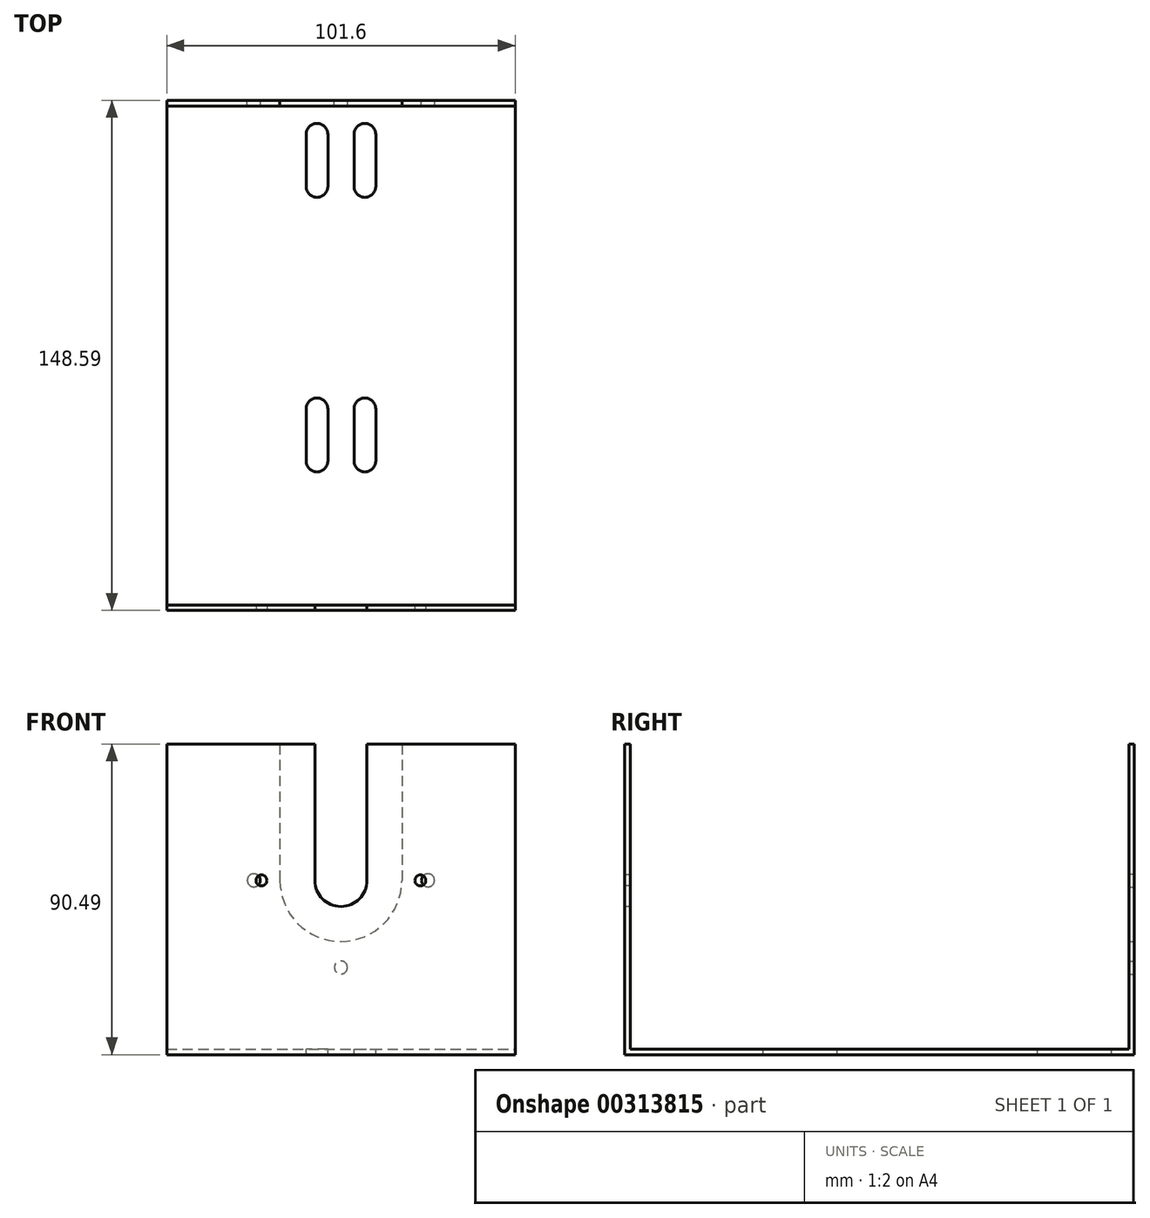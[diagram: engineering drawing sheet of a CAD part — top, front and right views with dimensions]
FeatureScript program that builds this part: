
annotation { "Feature Type Name" : "Feature", "Feature Type Description" : "" }
export const myFeature = defineFeature(function(context is Context, id is Id, definition is map)
    precondition{}
    {
        {
            var Q0;
            Q0=qCreatedBy(makeId("Top.planeOp"),FACE);
            var sketch = newSketch(context, id + "F0", { "sketchPlane" : qUnion([Q0])});
            skLineSegment(sketch, "E0.bottom", {"start": v(0, 0) * mm, "end": v(101.6, 0) * mm});
            skLineSegment(sketch, "E0.top", {"start": v(0, 148.6) * mm, "end": v(101.6, 148.6) * mm});
            skLineSegment(sketch, "E0.left", {"start": v(0, 0) * mm, "end": v(0, 148.6) * mm});
            skLineSegment(sketch, "E0.right", {"start": v(101.6, 0) * mm, "end": v(101.6, 148.6) * mm});
            skSolve(sketch);
        }
        {
            var Q0;
            Q0 = qSketchRegion(id + "F0", true);
            extrude(context, id + "F1", {"entities" : qUnion([Q0]), "depth" : 1.59 * mm});
        }
        {
            var Q0;
            Q0=makeQuery(id+"F1.opExtrude","CAP_FACE",FACE,{"disambiguationData":[OSD([sQuery(id+"F0.wireOp",EDGE,"E0.bottom"),sQuery(id+"F0.wireOp",EDGE,"E0.top"),sQuery(id+"F0.wireOp",EDGE,"E0.left"),sQuery(id+"F0.wireOp",EDGE,"E0.right")])],"isStart":false});
            var sketch = newSketch(context, id + "F2", { "sketchPlane" : qUnion([Q0])});
            skLineSegment(sketch, "E1.bottom", {"start": v(0, 148.6) * mm, "end": v(101.6, 148.6) * mm});
            skLineSegment(sketch, "E1.top", {"start": v(0, 147) * mm, "end": v(101.6, 147) * mm});
            skLineSegment(sketch, "E1.left", {"start": v(0, 148.6) * mm, "end": v(0, 147) * mm});
            skLineSegment(sketch, "E1.right", {"start": v(101.6, 148.6) * mm, "end": v(101.6, 147) * mm});
            skLineSegment(sketch, "E2.bottom", {"start": v(0, 0) * mm, "end": v(101.6, 0) * mm});
            skLineSegment(sketch, "E2.top", {"start": v(0, 1.59) * mm, "end": v(101.6, 1.59) * mm});
            skLineSegment(sketch, "E2.left", {"start": v(0, 0) * mm, "end": v(0, 1.59) * mm});
            skLineSegment(sketch, "E2.right", {"start": v(101.6, 0) * mm, "end": v(101.6, 1.59) * mm});
            skSolve(sketch);
        }
        {
            var Q0;
            Q0 = qSketchRegion(id + "F2", true);
            extrude(context, id + "F3", {"entities" : qUnion([Q0]), "operationType" : NewBodyOperationType.ADD, "depth" : 88.9 * mm});
        }
        {
            var Q0;
            Q0=makeQuery(id+"F3.boolean.opBoolean","MERGE",FACE,{"derivedFrom":[makeQuery(id+"F1.opExtrude","SWEPT_FACE",FACE,{"disambiguationData":[OSD([sQuery(id+"F0.wireOp",EDGE,"E0.top")])]}),makeQuery(id+"F3.opExtrude","SWEPT_FACE",FACE,{"disambiguationData":[OSD([sQuery(id+"F2.wireOp",EDGE,"E1.bottom")])]})]});
            var sketch = newSketch(context, id + "F4", { "sketchPlane" : qUnion([Q0])});
            skCircle(sketch, "E3", {"center": v(-50.8, 50.8) * mm, "radius": 38.1 * mm, "construction": true});
            skPoint(sketch, "E3.centerSnap0", {"position": v(-50.8, 90.49) * mm});
            skSolve(sketch);
        }
        {
            var Q0;
            {var subQ0=sQuery(id+"F0.wireOp",EDGE,"E0.top");Q0=makeQuery(id+"F4.imprint","IMPRINT",FACE,{"disambiguationData":[TD([[makeQuery(id+"F4.imprint","IMPRINT",EDGE,{"derivedFrom":makeQuery(id+"F1.opExtrude","CAP_EDGE",EDGE,{"disambiguationData":[OSD([subQ0])],"isStart":true})}),-1.0]])]});}
            var sketch = newSketch(context, id + "F5", { "sketchPlane" : qUnion([Q0])});
            skCircle(sketch, "E4.0", {"center": v(-50.8, 50.8) * mm, "radius": 38.1 * mm, "construction": true});
            skLineSegment(sketch, "E5", {"start": v(-50.8, -11.96) * mm, "end": v(-50.8, 107.1) * mm, "construction": true});
            skCircle(sketch, "E6", {"center": v(-50.8, 50.8) * mm, "radius": 17.78 * mm});
            skLineSegment(sketch, "E7", {"start": v(-68.58, 50.8) * mm, "end": v(-68.58, 90.49) * mm});
            skLineSegment(sketch, "E8", {"start": v(-33.02, 50.8) * mm, "end": v(-33.02, 90.49) * mm});
            skLineSegment(sketch, "E9", {"start": v(-68.58, 90.49) * mm, "end": v(-33.02, 90.49) * mm});
            skLineSegment(sketch, "E10", {"start": v(-105.94, 50.8) * mm, "end": v(8.17, 50.8) * mm, "construction": true});
            skCircle(sketch, "E11", {"center": v(-50.8, 25.4) * mm, "radius": 1.9 * mm});
            skCircle(sketch, "E12", {"center": v(-25.4, 50.8) * mm, "radius": 1.9 * mm});
            skCircle(sketch, "E13", {"center": v(-76.2, 50.8) * mm, "radius": 1.9 * mm});
            skSolve(sketch);
        }
        {
            var Q0;
            Q0 = qSketchRegion(id + "F5", true);
            extrude(context, id + "F6", {"entities" : qUnion([Q0]), "operationType" : NewBodyOperationType.REMOVE, "endBound" : BoundingType.UP_TO_NEXT, "oppositeDirection" : true, "depth" : 25.4 * mm});
        }
        {
            var Q0;
            Q0=makeQuery(id+"F3.boolean.opBoolean","MERGE",FACE,{"derivedFrom":[makeQuery(id+"F1.opExtrude","SWEPT_FACE",FACE,{"disambiguationData":[OSD([sQuery(id+"F0.wireOp",EDGE,"E0.bottom")])]}),makeQuery(id+"F3.opExtrude","SWEPT_FACE",FACE,{"disambiguationData":[OSD([sQuery(id+"F2.wireOp",EDGE,"E2.bottom")])]})]});
            var sketch = newSketch(context, id + "F7", { "sketchPlane" : qUnion([Q0])});
            skCircle(sketch, "E14.0", {"center": v(50.8, 50.8) * mm, "radius": 38.1 * mm, "construction": true});
            skCircle(sketch, "E15", {"center": v(50.8, 50.8) * mm, "radius": 7.62 * mm});
            skLineSegment(sketch, "E16", {"start": v(43.18, 50.8) * mm, "end": v(43.18, 90.49) * mm});
            skLineSegment(sketch, "E17", {"start": v(58.42, 50.8) * mm, "end": v(58.42, 90.49) * mm});
            skLineSegment(sketch, "E18", {"start": v(58.42, 90.49) * mm, "end": v(43.18, 90.49) * mm});
            skLineSegment(sketch, "E19", {"start": v(50.8, 96.93) * mm, "end": v(50.8, -8.53) * mm, "construction": true});
            skPoint(sketch, "E19.endSnap0", {"position": v(50.8, 5.08) * mm});
            skLineSegment(sketch, "E20", {"start": v(-8.65, 50.8) * mm, "end": v(115.7, 50.8) * mm, "construction": true});
            skCircle(sketch, "E21", {"center": v(73.98, 50.8) * mm, "radius": 1.59 * mm});
            skCircle(sketch, "E22.MirrorC", {"center": v(27.62, 50.8) * mm, "radius": 1.59 * mm});
            skSolve(sketch);
        }
        {
            var Q0;
            Q0 = qSketchRegion(id + "F7", true);
            extrude(context, id + "F8", {"entities" : qUnion([Q0]), "operationType" : NewBodyOperationType.REMOVE, "endBound" : BoundingType.UP_TO_NEXT, "oppositeDirection" : true, "depth" : 25.4 * mm});
        }
        {
            var Q0;
            Q0=makeQuery(id+"F1.opExtrude","CAP_FACE",FACE,{"disambiguationData":[OSD([sQuery(id+"F0.wireOp",EDGE,"E0.bottom"),sQuery(id+"F0.wireOp",EDGE,"E0.top"),sQuery(id+"F0.wireOp",EDGE,"E0.left"),sQuery(id+"F0.wireOp",EDGE,"E0.right")])],"isStart":false});
            var sketch = newSketch(context, id + "F9", { "sketchPlane" : qUnion([Q0])});
            skLineSegment(sketch, "E23", {"start": v(50.8, 141.92) * mm, "end": v(50.8, 6.67) * mm, "construction": true});
            skLineSegment(sketch, "E24", {"start": v(0, 40.32) * mm, "end": v(101.6, 40.32) * mm, "construction": true});
            skLineSegment(sketch, "E25", {"start": v(50.8, 49.85) * mm, "end": v(38.1, 49.85) * mm, "construction": true});
            skLineSegment(sketch, "E26", {"start": v(50.8, 43.5) * mm, "end": v(38.1, 43.5) * mm, "construction": true});
            skLineSegment(sketch, "E27", {"start": v(50.8, 40.32) * mm, "end": v(50.8, 141.92) * mm, "construction": true});
            skLineSegment(sketch, "E28", {"start": v(0, 91.12) * mm, "end": v(101.6, 91.12) * mm, "construction": true});
            skPoint(sketch, "E28.startSnap0", {"position": v(50.8, 91.12) * mm});
            skArc(sketch, "E29", {"start": v(38.1, 49.85) * mm, "mid": v(34.92, 46.67) * mm, "end": v(38.1, 43.5) * mm, "construction": true});
            skLineSegment(sketch, "E30.MirrorCS", {"start": v(50.8, 49.85) * mm, "end": v(63.5, 49.85) * mm, "construction": true});
            skLineSegment(sketch, "E31.MirrorCS", {"start": v(50.8, 43.5) * mm, "end": v(63.5, 43.5) * mm, "construction": true});
            skArc(sketch, "E32.MirrorCS", {"start": v(63.5, 49.85) * mm, "mid": v(66.68, 46.67) * mm, "end": v(63.5, 43.5) * mm, "construction": true});
            skArc(sketch, "E33.MirrorCS", {"start": v(63.5, 132.4) * mm, "mid": v(66.68, 135.57) * mm, "end": v(63.5, 138.75) * mm, "construction": true});
            skLineSegment(sketch, "E34.MirrorCS", {"start": v(50.8, 138.75) * mm, "end": v(63.5, 138.75) * mm, "construction": true});
            skArc(sketch, "E35.MirrorCS", {"start": v(38.1, 132.4) * mm, "mid": v(34.92, 135.57) * mm, "end": v(38.1, 138.75) * mm, "construction": true});
            skLineSegment(sketch, "E36.MirrorCS", {"start": v(50.8, 138.75) * mm, "end": v(38.1, 138.75) * mm, "construction": true});
            skLineSegment(sketch, "E37.MirrorCS", {"start": v(50.8, 132.4) * mm, "end": v(38.1, 132.4) * mm, "construction": true});
            skLineSegment(sketch, "E38.MirrorCS", {"start": v(50.8, 132.4) * mm, "end": v(63.5, 132.4) * mm, "construction": true});
            skLineSegment(sketch, "E39.bottom", {"start": v(40.64, 138.75) * mm, "end": v(46.99, 138.75) * mm});
            skLineSegment(sketch, "E39.top", {"start": v(40.64, 123.5) * mm, "end": v(46.99, 123.5) * mm});
            skLineSegment(sketch, "E39.left", {"start": v(40.64, 138.75) * mm, "end": v(40.64, 123.5) * mm});
            skLineSegment(sketch, "E39.right", {"start": v(46.99, 138.75) * mm, "end": v(46.99, 123.5) * mm});
            skArc(sketch, "E40", {"start": v(46.99, 138.75) * mm, "mid": v(43.81, 141.92) * mm, "end": v(40.64, 138.75) * mm});
            skArc(sketch, "E41", {"start": v(40.64, 123.5) * mm, "mid": v(43.81, 120.33) * mm, "end": v(46.99, 123.5) * mm});
            skLineSegment(sketch, "E42.MirrorCS", {"start": v(60.96, 138.75) * mm, "end": v(54.61, 138.75) * mm});
            skLineSegment(sketch, "E43.MirrorCS", {"start": v(54.61, 138.75) * mm, "end": v(54.61, 123.5) * mm});
            skArc(sketch, "E44.MirrorCS", {"start": v(60.96, 123.5) * mm, "mid": v(57.79, 120.33) * mm, "end": v(54.61, 123.5) * mm});
            skArc(sketch, "E45.MirrorCS", {"start": v(54.61, 138.75) * mm, "mid": v(57.79, 141.92) * mm, "end": v(60.96, 138.75) * mm});
            skLineSegment(sketch, "E46.MirrorCS", {"start": v(60.96, 138.75) * mm, "end": v(60.96, 123.5) * mm});
            skLineSegment(sketch, "E47.MirrorCS", {"start": v(60.96, 123.5) * mm, "end": v(54.61, 123.5) * mm});
            skLineSegment(sketch, "E48.MirrorCS", {"start": v(60.96, 43.5) * mm, "end": v(54.61, 43.5) * mm});
            skArc(sketch, "E49.MirrorCS", {"start": v(54.61, 43.5) * mm, "mid": v(57.79, 40.32) * mm, "end": v(60.96, 43.5) * mm});
            skLineSegment(sketch, "E50.MirrorCS", {"start": v(40.64, 43.5) * mm, "end": v(40.64, 58.74) * mm});
            skLineSegment(sketch, "E51.MirrorCS", {"start": v(47, 43.5) * mm, "end": v(47, 58.74) * mm});
            skLineSegment(sketch, "E52.MirrorCS", {"start": v(54.61, 43.5) * mm, "end": v(54.61, 58.74) * mm});
            skLineSegment(sketch, "E53.MirrorCS", {"start": v(60.96, 43.5) * mm, "end": v(60.96, 58.74) * mm});
            skArc(sketch, "E54.MirrorCS", {"start": v(40.64, 58.74) * mm, "mid": v(43.82, 61.91) * mm, "end": v(47, 58.74) * mm});
            skLineSegment(sketch, "E55.MirrorCS", {"start": v(40.64, 58.74) * mm, "end": v(47, 58.74) * mm});
            skLineSegment(sketch, "E56.MirrorCS", {"start": v(60.96, 58.74) * mm, "end": v(54.61, 58.74) * mm});
            skArc(sketch, "E57.MirrorCS", {"start": v(60.96, 58.74) * mm, "mid": v(57.79, 61.91) * mm, "end": v(54.61, 58.74) * mm});
            skArc(sketch, "E58.MirrorCS", {"start": v(47, 43.5) * mm, "mid": v(43.82, 40.32) * mm, "end": v(40.64, 43.5) * mm});
            skLineSegment(sketch, "E59.MirrorCS", {"start": v(40.64, 43.5) * mm, "end": v(47, 43.5) * mm});
            skSolve(sketch);
        }
        {
            var Q0;
            Q0 = qSketchRegion(id + "F9", true);
            extrude(context, id + "F10", {"entities" : qUnion([Q0]), "operationType" : NewBodyOperationType.REMOVE, "endBound" : BoundingType.UP_TO_NEXT, "oppositeDirection" : true, "depth" : 25.4 * mm});
        }
    });
